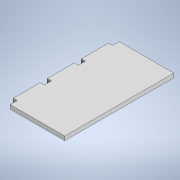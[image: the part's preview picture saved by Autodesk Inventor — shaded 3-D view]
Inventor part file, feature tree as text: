
AUTODESK INVENTOR PART (.ipt)
format: ipt  version: 2022 (Build 260153000, 153)  size: 108,544 bytes
history: native  units: mm
features: extrude x1, sketch x1
ambient origin geometry x8: Origin, YZ Plane, XZ Plane, XY Plane, X Axis, Y Axis, Z Axis, Center Point
bodies: Solid1 (feature_tree)
feature tree (2):
  extrude  "Extrusion1"  Depth=80.0mm
  sketch  "Sketch1"  dims[d0=40.0mm d1=80.0mm d2=5.0mm d3=3.0mm d4=20.0mm d5=5.0mm d6=20.0mm d7=5.0mm d8=20.0mm d9=3.0mm d10=0.0mm]
